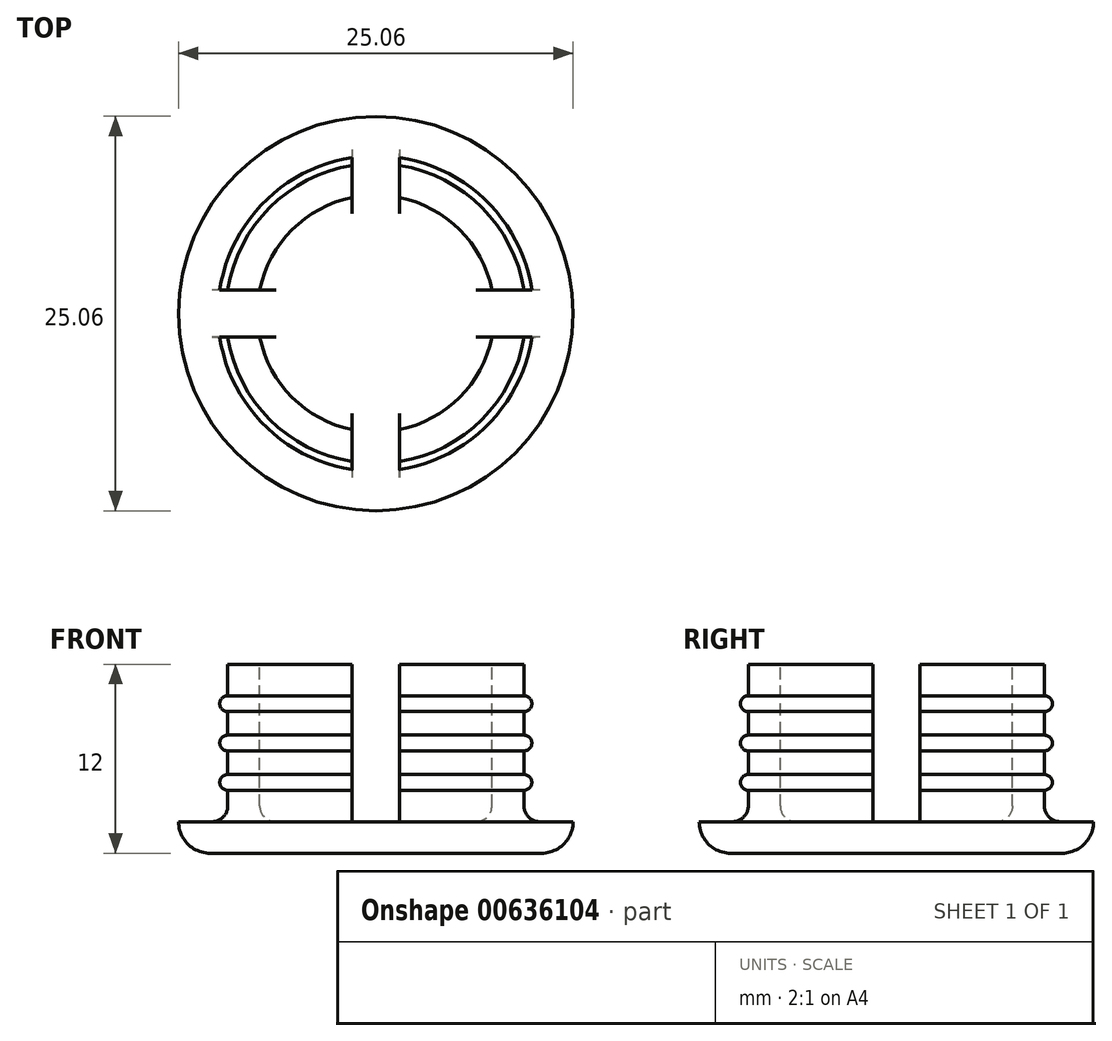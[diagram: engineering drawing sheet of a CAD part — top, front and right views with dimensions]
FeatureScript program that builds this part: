
annotation { "Feature Type Name" : "Feature", "Feature Type Description" : "" }
export const myFeature = defineFeature(function(context is Context, id is Id, definition is map)
    precondition{}
    {
        {
            var Q0;
            Q0=qCreatedBy(makeId("Right.planeOp"),FACE);
            var sketch = newSketch(context, id + "F0", { "sketchPlane" : qUnion([Q0])});
            skLineSegment(sketch, "E0", {"start": v(0, 18.97) * mm, "end": v(0, 0) * mm, "construction": true});
            skLineSegment(sketch, "E1", {"start": v(0, 0) * mm, "end": v(-10.52, 0) * mm});
            skLineSegment(sketch, "E2", {"start": v(-12.52, 2) * mm, "end": v(-12.52, 2) * mm});
            skLineSegment(sketch, "E3", {"start": v(-12.52, 2) * mm, "end": v(-9.52, 2) * mm});
            skLineSegment(sketch, "E4", {"start": v(-9.52, 2) * mm, "end": v(-9.52, 4) * mm});
            skLineSegment(sketch, "E5", {"start": v(-9.53, 12) * mm, "end": v(-7.52, 12) * mm});
            skLineSegment(sketch, "E6", {"start": v(-7.52, 12) * mm, "end": v(-7.52, 2) * mm});
            skLineSegment(sketch, "E7", {"start": v(-7.52, 2) * mm, "end": v(0, 2) * mm});
            skPoint(sketch, "E8.visualSharp", {"position": v(-12.52, 0) * mm});
            skArc(sketch, "E8.filletArc", {"start": v(-12.52, 2) * mm, "mid": v(-11.94, 0.59) * mm, "end": v(-10.52, 0) * mm});
            skLineSegment(sketch, "E9", {"start": v(0, 2) * mm, "end": v(0, 0) * mm});
            skArc(sketch, "E10", {"start": v(-9.52, 10) * mm, "mid": v(-10.02, 9.5) * mm, "end": v(-9.52, 9) * mm});
            skArc(sketch, "E11", {"start": v(-9.52, 5) * mm, "mid": v(-10.02, 4.5) * mm, "end": v(-9.52, 4) * mm});
            skArc(sketch, "E12", {"start": v(-9.52, 7.5) * mm, "mid": v(-10.02, 7) * mm, "end": v(-9.52, 6.5) * mm});
            skLineSegment(sketch, "E13.trimOffspring", {"start": v(-9.52, 10) * mm, "end": v(-9.52, 12) * mm});
            skLineSegment(sketch, "E14.trimOffspring", {"start": v(-9.52, 5) * mm, "end": v(-9.52, 6.5) * mm});
            skLineSegment(sketch, "E15", {"start": v(-9.52, 9) * mm, "end": v(-9.52, 7.5) * mm});
            skSolve(sketch);
        }
        {
            var Q0;
            Q0 = qSketchRegion(id + "F0", true);
            var Q1;
            Q1=sQuery(id+"F0.wireOp",EDGE,"E0");
            revolve(context, id + "F1", {"entities" : qUnion([Q0]), "axis" : qUnion([Q1]), "revolveType" : RevolveType.FULL});
        }
        {
            var Q0;
            Q0=makeQuery(id+"F1.opRevolve","SWEPT_FACE",FACE,{"disambiguationData":[OSD([sQuery(id+"F0.wireOp",EDGE,"E5")])]});
            var sketch = newSketch(context, id + "F2", { "sketchPlane" : qUnion([Q0])});
            skLineSegment(sketch, "E16.bottom", {"start": v(1.5, 11.44) * mm, "end": v(-1.5, 11.44) * mm});
            skLineSegment(sketch, "E16.top", {"start": v(1.5, -11.44) * mm, "end": v(-1.5, -11.44) * mm});
            skLineSegment(sketch, "E16.left", {"start": v(1.5, 11.44) * mm, "end": v(1.5, -11.44) * mm});
            skLineSegment(sketch, "E16.right", {"start": v(-1.5, 11.44) * mm, "end": v(-1.5, -11.44) * mm});
            skPoint(sketch, "E16.middle", {"position": v(0, 0) * mm});
            skLineSegment(sketch, "E17.bottom", {"start": v(12.18, -1.5) * mm, "end": v(-12.18, -1.5) * mm});
            skLineSegment(sketch, "E17.top", {"start": v(12.18, 1.5) * mm, "end": v(-12.18, 1.5) * mm});
            skLineSegment(sketch, "E17.left", {"start": v(12.18, -1.5) * mm, "end": v(12.18, 1.5) * mm});
            skLineSegment(sketch, "E17.right", {"start": v(-12.18, -1.5) * mm, "end": v(-12.18, 1.5) * mm});
            skSolve(sketch);
        }
        {
            var Q0;
            Q0 = qSketchRegion(id + "F2", true);
            var Q1;
            Q1=makeQuery(id+"F1.opRevolve","SWEPT_FACE",FACE,{"disambiguationData":[OSD([sQuery(id+"F0.wireOp",EDGE,"E3")])]});
            extrude(context, id + "F3", {"entities" : qUnion([Q0]), "operationType" : NewBodyOperationType.REMOVE, "endBound" : BoundingType.UP_TO_SURFACE, "oppositeDirection" : true, "depth" : 25 * mm, "endBoundEntityFace" : qUnion([Q1]), "offsetDistance" : 25 * mm});
        }
        {
            var Q0;
            {var subQ1=sQuery(id+"F2.wireOp",EDGE,"E17.top");var subQ2=sQuery(id+"F0.wireOp",EDGE,"E5");var subQ3=makeQuery(id+"F1.opRevolve","SWEPT_EDGE",EDGE,{"disambiguationData":[OSD([subQ2,sQuery(id+"F0.wireOp",EDGE,"E13.trimOffspring")])]});var subQ5=sQuery(id+"F0.wireOp",EDGE,"E6");var subQ8=sQuery(id+"F2.wireOp",EDGE,"E16.right");var subQ9=makeQuery(id+"F2.imprint","INTERSECT",VERTEX,{"derivedFrom":[subQ8,subQ1]});var subQ10=sQuery(id+"F0.wireOp",EDGE,"E7");var subQ12=makeQuery(id+"F2.imprint","INTERSECT",VERTEX,{"disambiguationData":[OD(0.0)],"derivedFrom":[subQ3,subQ8]});Q0=makeQuery(id+"F3.boolean.opBoolean","SPLIT",EDGE,{"disambiguationData":[TD([makeQuery(id+"F3.opExtrude","SWEPT_FACE",FACE,{"disambiguationData":[OSD([subQ8]),TDD([makeQuery(id+"F2.imprint","IMPRINT",EDGE,{"disambiguationData":[TD([[makeQuery(id+"F2.imprint","INTERSECT",VERTEX,{"derivedFrom":[sQuery(id+"F2.wireOp",EDGE,"E16.bottom"),subQ8]}),-1.0]])],"derivedFrom":subQ8}),makeQuery(id+"F2.imprint","IMPRINT",EDGE,{"disambiguationData":[TD([[subQ12,-1.0]])],"derivedFrom":subQ8}),makeQuery(id+"F2.imprint","IMPRINT",EDGE,{"disambiguationData":[TD([[subQ9,1.0]])],"derivedFrom":subQ8})])]})])],"derivedFrom":makeQuery(id+"F1.opRevolve","SWEPT_EDGE",EDGE,{"disambiguationData":[OSD([subQ5,subQ10])]})});}
            var Q1;
            {var subQ1=sQuery(id+"F0.wireOp",EDGE,"E7");var subQ2=sQuery(id+"F0.wireOp",EDGE,"E6");var subQ3=sQuery(id+"F2.wireOp",EDGE,"E16.right");var subQ4=sQuery(id+"F0.wireOp",EDGE,"E5");var subQ5=makeQuery(id+"F1.opRevolve","SWEPT_EDGE",EDGE,{"disambiguationData":[OSD([subQ4,sQuery(id+"F0.wireOp",EDGE,"E13.trimOffspring")])]});var subQ6=makeQuery(id+"F2.imprint","INTERSECT",VERTEX,{"disambiguationData":[OD(1.0)],"derivedFrom":[subQ5,subQ3]});var subQ9=sQuery(id+"F2.wireOp",EDGE,"E17.bottom");var subQ10=makeQuery(id+"F2.imprint","INTERSECT",VERTEX,{"derivedFrom":[subQ3,subQ9]});Q1=makeQuery(id+"F3.boolean.opBoolean","SPLIT",EDGE,{"disambiguationData":[TD([makeQuery(id+"F3.opExtrude","SWEPT_FACE",FACE,{"disambiguationData":[OSD([subQ3]),TDD([makeQuery(id+"F2.imprint","IMPRINT",EDGE,{"disambiguationData":[TD([[subQ10,-1.0]])],"derivedFrom":subQ3}),makeQuery(id+"F2.imprint","IMPRINT",EDGE,{"disambiguationData":[TD([[subQ6,1.0]])],"derivedFrom":subQ3}),makeQuery(id+"F2.imprint","IMPRINT",EDGE,{"disambiguationData":[TD([[makeQuery(id+"F2.imprint","INTERSECT",VERTEX,{"derivedFrom":[sQuery(id+"F2.wireOp",EDGE,"E16.top"),subQ3]}),1.0]])],"derivedFrom":subQ3})])]})])],"derivedFrom":makeQuery(id+"F1.opRevolve","SWEPT_EDGE",EDGE,{"disambiguationData":[OSD([subQ2,subQ1])]})});}
            var Q2;
            {var subQ1=sQuery(id+"F0.wireOp",EDGE,"E7");var subQ2=sQuery(id+"F2.wireOp",EDGE,"E17.top");var subQ3=sQuery(id+"F2.wireOp",EDGE,"E16.left");var subQ4=makeQuery(id+"F2.imprint","INTERSECT",VERTEX,{"derivedFrom":[subQ3,subQ2]});var subQ5=sQuery(id+"F0.wireOp",EDGE,"E6");var subQ6=sQuery(id+"F0.wireOp",EDGE,"E5");var subQ9=makeQuery(id+"F1.opRevolve","SWEPT_EDGE",EDGE,{"disambiguationData":[OSD([subQ6,sQuery(id+"F0.wireOp",EDGE,"E13.trimOffspring")])]});var subQ10=makeQuery(id+"F2.imprint","INTERSECT",VERTEX,{"disambiguationData":[OD(0.0)],"derivedFrom":[subQ9,subQ3]});Q2=makeQuery(id+"F3.boolean.opBoolean","SPLIT",EDGE,{"disambiguationData":[TD([makeQuery(id+"F3.opExtrude","SWEPT_FACE",FACE,{"disambiguationData":[OSD([subQ3]),TDD([makeQuery(id+"F2.imprint","IMPRINT",EDGE,{"disambiguationData":[TD([[makeQuery(id+"F2.imprint","INTERSECT",VERTEX,{"derivedFrom":[sQuery(id+"F2.wireOp",EDGE,"E16.bottom"),subQ3]}),-1.0]])],"derivedFrom":subQ3}),makeQuery(id+"F2.imprint","IMPRINT",EDGE,{"disambiguationData":[TD([[subQ10,-1.0]])],"derivedFrom":subQ3}),makeQuery(id+"F2.imprint","IMPRINT",EDGE,{"disambiguationData":[TD([[subQ4,1.0]])],"derivedFrom":subQ3})])]})])],"derivedFrom":makeQuery(id+"F1.opRevolve","SWEPT_EDGE",EDGE,{"disambiguationData":[OSD([subQ5,subQ1])]})});}
            var Q3;
            {var subQ1=sQuery(id+"F0.wireOp",EDGE,"E7");var subQ2=sQuery(id+"F0.wireOp",EDGE,"E6");var subQ3=sQuery(id+"F2.wireOp",EDGE,"E16.left");var subQ4=sQuery(id+"F0.wireOp",EDGE,"E5");var subQ5=makeQuery(id+"F1.opRevolve","SWEPT_EDGE",EDGE,{"disambiguationData":[OSD([subQ4,sQuery(id+"F0.wireOp",EDGE,"E13.trimOffspring")])]});var subQ6=makeQuery(id+"F2.imprint","INTERSECT",VERTEX,{"disambiguationData":[OD(1.0)],"derivedFrom":[subQ5,subQ3]});var subQ9=sQuery(id+"F2.wireOp",EDGE,"E17.bottom");var subQ10=makeQuery(id+"F2.imprint","INTERSECT",VERTEX,{"derivedFrom":[subQ3,subQ9]});Q3=makeQuery(id+"F3.boolean.opBoolean","SPLIT",EDGE,{"disambiguationData":[TD([makeQuery(id+"F3.opExtrude","SWEPT_FACE",FACE,{"disambiguationData":[OSD([subQ3]),TDD([makeQuery(id+"F2.imprint","IMPRINT",EDGE,{"disambiguationData":[TD([[subQ10,-1.0]])],"derivedFrom":subQ3}),makeQuery(id+"F2.imprint","IMPRINT",EDGE,{"disambiguationData":[TD([[subQ6,1.0]])],"derivedFrom":subQ3}),makeQuery(id+"F2.imprint","IMPRINT",EDGE,{"disambiguationData":[TD([[makeQuery(id+"F2.imprint","INTERSECT",VERTEX,{"derivedFrom":[sQuery(id+"F2.wireOp",EDGE,"E16.top"),subQ3]}),1.0]])],"derivedFrom":subQ3})])]})])],"derivedFrom":makeQuery(id+"F1.opRevolve","SWEPT_EDGE",EDGE,{"disambiguationData":[OSD([subQ2,subQ1])]})});}
            var Q4;
            {var subQ0=sQuery(id+"F0.wireOp",EDGE,"E3");var subQ1=sQuery(id+"F2.wireOp",EDGE,"E17.top");var subQ2=sQuery(id+"F0.wireOp",EDGE,"E5");var subQ3=makeQuery(id+"F1.opRevolve","SWEPT_EDGE",EDGE,{"disambiguationData":[OSD([subQ2,sQuery(id+"F0.wireOp",EDGE,"E13.trimOffspring")])]});var subQ7=sQuery(id+"F2.wireOp",EDGE,"E16.right");var subQ8=makeQuery(id+"F2.imprint","INTERSECT",VERTEX,{"derivedFrom":[subQ7,subQ1]});var subQ9=sQuery(id+"F0.wireOp",EDGE,"E4");var subQ11=makeQuery(id+"F2.imprint","INTERSECT",VERTEX,{"disambiguationData":[OD(0.0)],"derivedFrom":[subQ3,subQ7]});Q4=makeQuery(id+"F3.boolean.opBoolean","SPLIT",EDGE,{"disambiguationData":[TD([makeQuery(id+"F3.opExtrude","SWEPT_FACE",FACE,{"disambiguationData":[OSD([subQ7]),TDD([makeQuery(id+"F2.imprint","IMPRINT",EDGE,{"disambiguationData":[TD([[makeQuery(id+"F2.imprint","INTERSECT",VERTEX,{"derivedFrom":[sQuery(id+"F2.wireOp",EDGE,"E16.bottom"),subQ7]}),-1.0]])],"derivedFrom":subQ7}),makeQuery(id+"F2.imprint","IMPRINT",EDGE,{"disambiguationData":[TD([[subQ11,-1.0]])],"derivedFrom":subQ7}),makeQuery(id+"F2.imprint","IMPRINT",EDGE,{"disambiguationData":[TD([[subQ8,1.0]])],"derivedFrom":subQ7})])]})])],"derivedFrom":makeQuery(id+"F1.opRevolve","SWEPT_EDGE",EDGE,{"disambiguationData":[OSD([subQ0,subQ9])]})});}
            var Q5;
            {var subQ0=sQuery(id+"F0.wireOp",EDGE,"E3");var subQ1=sQuery(id+"F2.wireOp",EDGE,"E17.top");var subQ2=sQuery(id+"F2.wireOp",EDGE,"E16.left");var subQ3=makeQuery(id+"F2.imprint","INTERSECT",VERTEX,{"derivedFrom":[subQ2,subQ1]});var subQ4=sQuery(id+"F0.wireOp",EDGE,"E5");var subQ7=makeQuery(id+"F1.opRevolve","SWEPT_EDGE",EDGE,{"disambiguationData":[OSD([subQ4,sQuery(id+"F0.wireOp",EDGE,"E13.trimOffspring")])]});var subQ8=makeQuery(id+"F2.imprint","INTERSECT",VERTEX,{"disambiguationData":[OD(0.0)],"derivedFrom":[subQ7,subQ2]});var subQ9=sQuery(id+"F0.wireOp",EDGE,"E4");Q5=makeQuery(id+"F3.boolean.opBoolean","SPLIT",EDGE,{"disambiguationData":[TD([makeQuery(id+"F3.opExtrude","SWEPT_FACE",FACE,{"disambiguationData":[OSD([subQ2]),TDD([makeQuery(id+"F2.imprint","IMPRINT",EDGE,{"disambiguationData":[TD([[makeQuery(id+"F2.imprint","INTERSECT",VERTEX,{"derivedFrom":[sQuery(id+"F2.wireOp",EDGE,"E16.bottom"),subQ2]}),-1.0]])],"derivedFrom":subQ2}),makeQuery(id+"F2.imprint","IMPRINT",EDGE,{"disambiguationData":[TD([[subQ8,-1.0]])],"derivedFrom":subQ2}),makeQuery(id+"F2.imprint","IMPRINT",EDGE,{"disambiguationData":[TD([[subQ3,1.0]])],"derivedFrom":subQ2})])]})])],"derivedFrom":makeQuery(id+"F1.opRevolve","SWEPT_EDGE",EDGE,{"disambiguationData":[OSD([subQ0,subQ9])]})});}
            var Q6;
            {var subQ0=sQuery(id+"F0.wireOp",EDGE,"E3");var subQ1=sQuery(id+"F0.wireOp",EDGE,"E4");var subQ2=sQuery(id+"F2.wireOp",EDGE,"E16.left");var subQ3=sQuery(id+"F0.wireOp",EDGE,"E5");var subQ4=makeQuery(id+"F1.opRevolve","SWEPT_EDGE",EDGE,{"disambiguationData":[OSD([subQ3,sQuery(id+"F0.wireOp",EDGE,"E13.trimOffspring")])]});var subQ5=makeQuery(id+"F2.imprint","INTERSECT",VERTEX,{"disambiguationData":[OD(1.0)],"derivedFrom":[subQ4,subQ2]});var subQ8=sQuery(id+"F2.wireOp",EDGE,"E17.bottom");var subQ9=makeQuery(id+"F2.imprint","INTERSECT",VERTEX,{"derivedFrom":[subQ2,subQ8]});Q6=makeQuery(id+"F3.boolean.opBoolean","SPLIT",EDGE,{"disambiguationData":[TD([makeQuery(id+"F3.opExtrude","SWEPT_FACE",FACE,{"disambiguationData":[OSD([subQ2]),TDD([makeQuery(id+"F2.imprint","IMPRINT",EDGE,{"disambiguationData":[TD([[subQ9,-1.0]])],"derivedFrom":subQ2}),makeQuery(id+"F2.imprint","IMPRINT",EDGE,{"disambiguationData":[TD([[subQ5,1.0]])],"derivedFrom":subQ2}),makeQuery(id+"F2.imprint","IMPRINT",EDGE,{"disambiguationData":[TD([[makeQuery(id+"F2.imprint","INTERSECT",VERTEX,{"derivedFrom":[sQuery(id+"F2.wireOp",EDGE,"E16.top"),subQ2]}),1.0]])],"derivedFrom":subQ2})])]})])],"derivedFrom":makeQuery(id+"F1.opRevolve","SWEPT_EDGE",EDGE,{"disambiguationData":[OSD([subQ0,subQ1])]})});}
            var Q7;
            {var subQ0=sQuery(id+"F0.wireOp",EDGE,"E3");var subQ1=sQuery(id+"F0.wireOp",EDGE,"E4");var subQ2=sQuery(id+"F2.wireOp",EDGE,"E16.right");var subQ3=sQuery(id+"F0.wireOp",EDGE,"E5");var subQ4=makeQuery(id+"F1.opRevolve","SWEPT_EDGE",EDGE,{"disambiguationData":[OSD([subQ3,sQuery(id+"F0.wireOp",EDGE,"E13.trimOffspring")])]});var subQ5=makeQuery(id+"F2.imprint","INTERSECT",VERTEX,{"disambiguationData":[OD(1.0)],"derivedFrom":[subQ4,subQ2]});var subQ8=sQuery(id+"F2.wireOp",EDGE,"E17.bottom");var subQ9=makeQuery(id+"F2.imprint","INTERSECT",VERTEX,{"derivedFrom":[subQ2,subQ8]});Q7=makeQuery(id+"F3.boolean.opBoolean","SPLIT",EDGE,{"disambiguationData":[TD([makeQuery(id+"F3.opExtrude","SWEPT_FACE",FACE,{"disambiguationData":[OSD([subQ2]),TDD([makeQuery(id+"F2.imprint","IMPRINT",EDGE,{"disambiguationData":[TD([[subQ9,-1.0]])],"derivedFrom":subQ2}),makeQuery(id+"F2.imprint","IMPRINT",EDGE,{"disambiguationData":[TD([[subQ5,1.0]])],"derivedFrom":subQ2}),makeQuery(id+"F2.imprint","IMPRINT",EDGE,{"disambiguationData":[TD([[makeQuery(id+"F2.imprint","INTERSECT",VERTEX,{"derivedFrom":[sQuery(id+"F2.wireOp",EDGE,"E16.top"),subQ2]}),1.0]])],"derivedFrom":subQ2})])]})])],"derivedFrom":makeQuery(id+"F1.opRevolve","SWEPT_EDGE",EDGE,{"disambiguationData":[OSD([subQ0,subQ1])]})});}
            fillet(context, id + "F4", {"entities" : qUnion([Q0, Q1, Q2, Q3, Q4, Q5, Q6, Q7]), "radius" : 1 * mm, "tangentPropagation" : true, "allowEdgeOverflow" : false});
        }
    });
